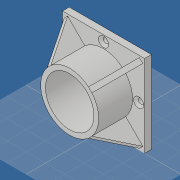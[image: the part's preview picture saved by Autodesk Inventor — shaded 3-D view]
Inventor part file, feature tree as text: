
AUTODESK INVENTOR PART (.ipt)
format: ipt  version: 2019 (Build 230136000, 136)  size: 169,472 bytes
history: native  units: mm
features: sketch x3, extrude x3, other x2, pattern_circular x2, plane x1, hole x1
ambient origin geometry x8: Origin, YZ Plane, XZ Plane, XY Plane, X Axis, Y Axis, Z Axis, Center Point
bodies: Volumenkörper1 (feature_tree)
feature tree (12):
  other  "<userpath>\OneDrive\Dokumente\Inventor\Absauganlage\Absauganlage_Params.xlsx"
  sketch  "Skizze1"  dims[d0=50.2mm d2=60.0mm]
  extrude  "Extrusion1"  Depth=60.0mm
  extrude  "Extrusion2"  Depth=35.0mm TaperAngle=0.0deg
  plane  "Arbeitsebene1"
  extrude  "Extrusion3"  Depth=85.0mm TaperAngle=360.0deg
  pattern_circular  "Runde Anordnung1"  [2 undecoded]
  hole  "Bohrung2"  [1 undecoded]
  pattern_circular  "Runde Anordnung3"  Angle=45.0deg  [1 undecoded]
  sketch  "Skizze2"  dims[d3=7.0mm d4=0.0mm d5=35.0mm d6=0.0mm]
  sketch  "Skizze3"  dims[d9=5.0mm d10=0.0mm d11=40.0mm d12=360.0deg d25=85.0mm d26=85.0mm d27=45.0deg d28=25.0mm d29=60.0mm d30=85.0mm d31=72.5mm d32=5.5mm d33=6.0mm d34=10.4mm d35=2.0mm d36=90.0deg d37=8.0mm d38=20.594885mm d39=40.0mm d40=360.0deg]
  other  "Schnittkanten projizieren1"
note: 4 required parameter values undecoded (feature->parameter linkage not recoverable at this tier; creation-order binding heuristic only, values carry confidence <= 0.55)
